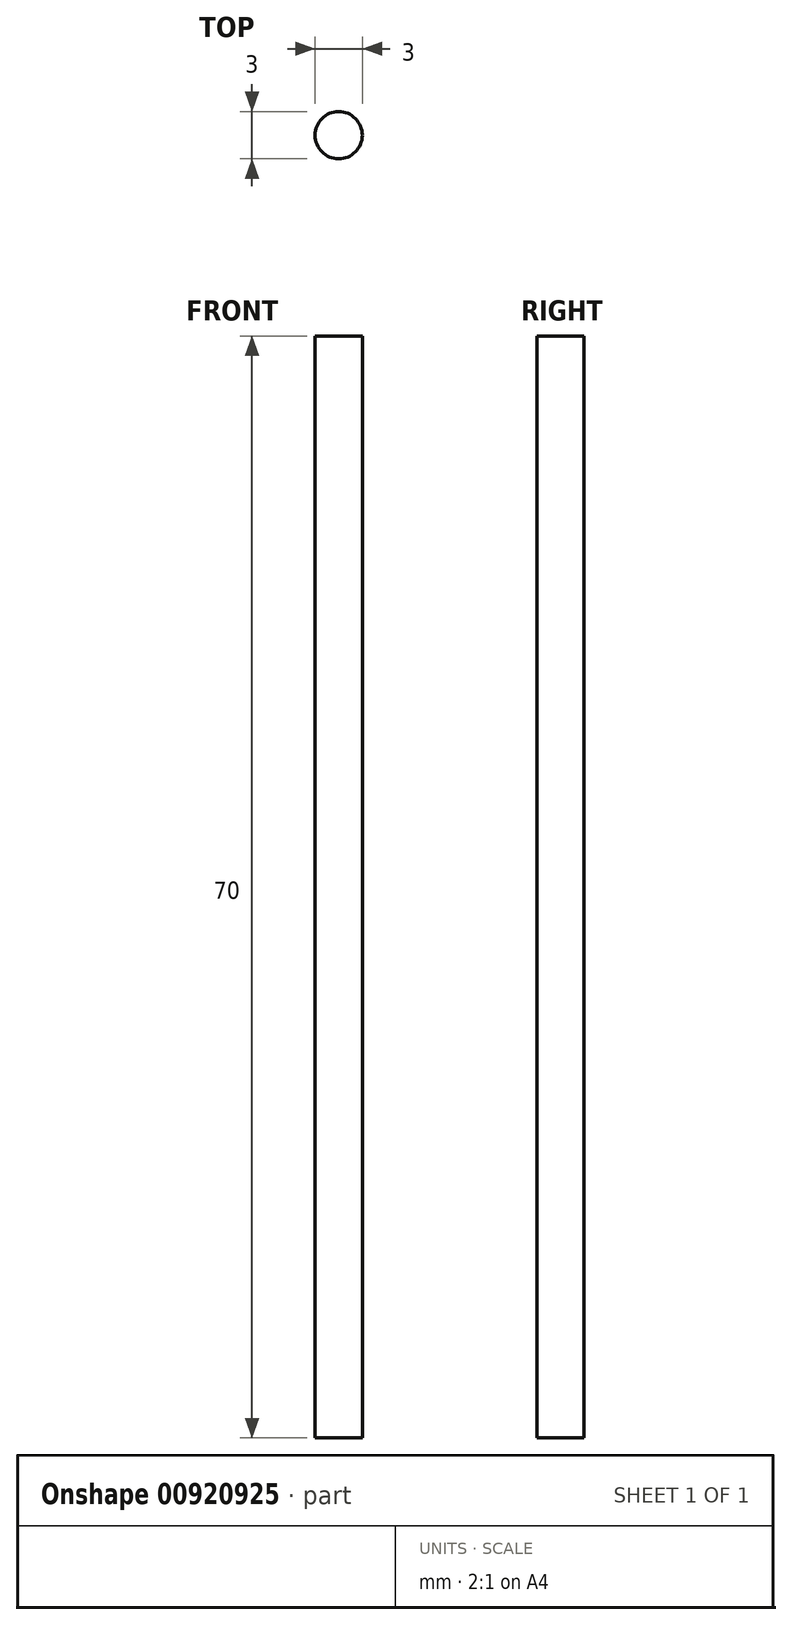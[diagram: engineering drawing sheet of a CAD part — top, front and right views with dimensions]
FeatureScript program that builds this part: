
annotation { "Feature Type Name" : "Feature", "Feature Type Description" : "" }
export const myFeature = defineFeature(function(context is Context, id is Id, definition is map)
    precondition{}
    {
        {
            var Q0;
            Q0=qCreatedBy(makeId("Top.planeOp"),FACE);
            var sketch = newSketch(context, id + "F0", { "sketchPlane" : qUnion([Q0])});
            skCircle(sketch, "E0", {"center": v(0, 0) * mm, "radius": 1.5 * mm});
            skSolve(sketch);
        }
        {
            var Q0;
            Q0 = qSketchRegion(id + "F0", true);
            extrude(context, id + "F1", {"entities" : qUnion([Q0]), "depth" : 70 * mm, "offsetDistance" : 25 * mm});
        }
    });
